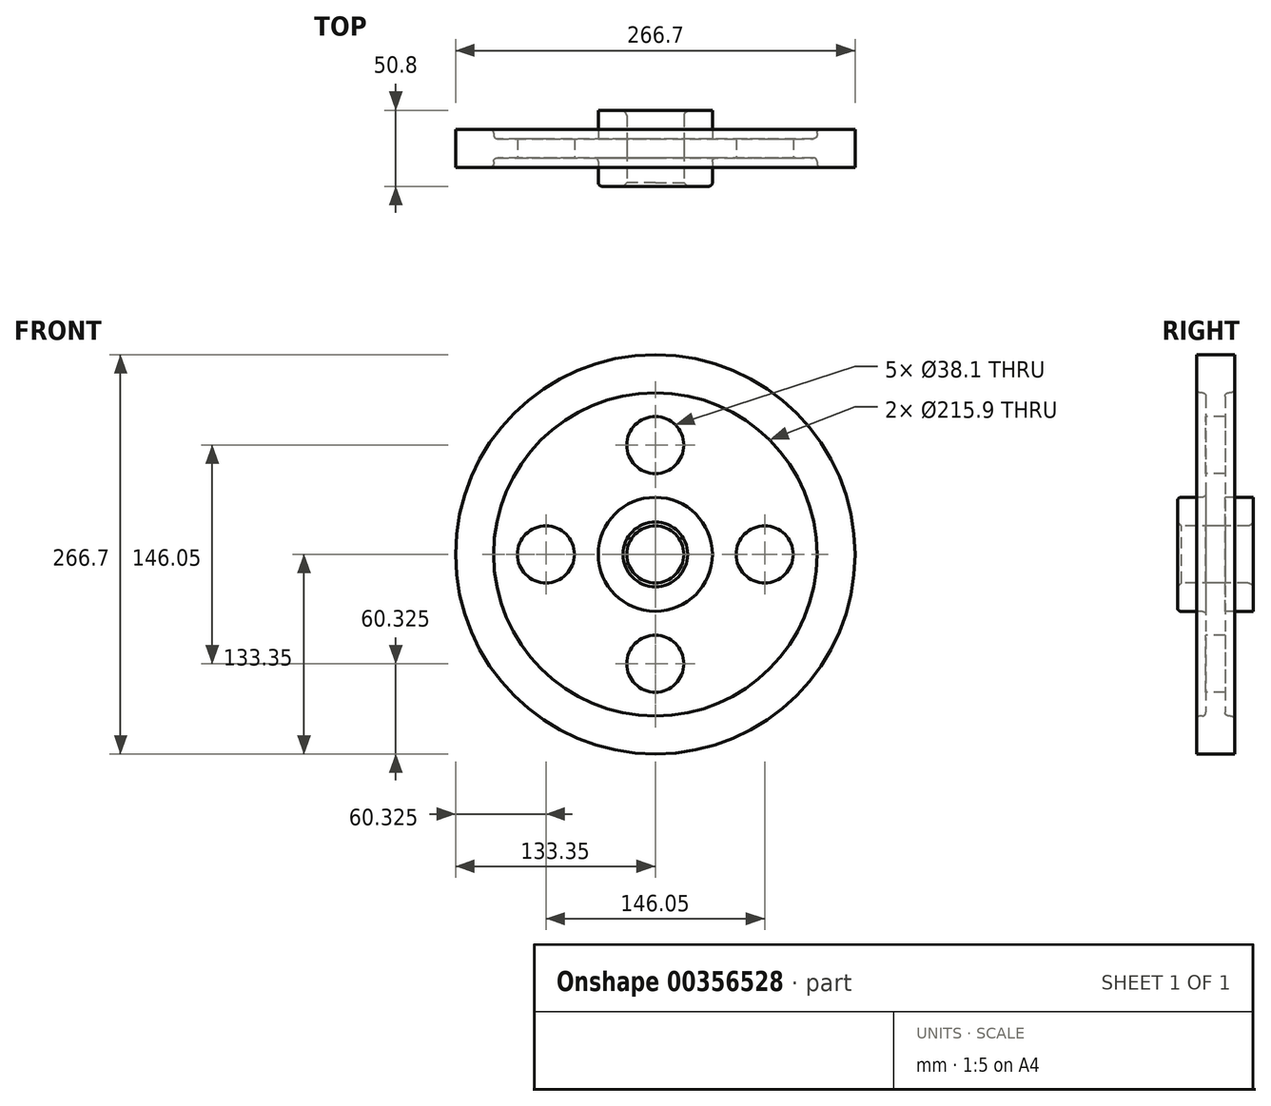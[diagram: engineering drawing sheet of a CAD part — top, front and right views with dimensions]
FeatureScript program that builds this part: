
annotation { "Feature Type Name" : "Feature", "Feature Type Description" : "" }
export const myFeature = defineFeature(function(context is Context, id is Id, definition is map)
    precondition{}
    {
        {
            var Q0;
            Q0=qCreatedBy(makeId("Right.planeOp"),FACE);
            var sketch = newSketch(context, id + "F0", { "sketchPlane" : qUnion([Q0])});
            skLineSegment(sketch, "E0", {"start": v(0, 0) * mm, "end": v(25.4, 0) * mm});
            skLineSegment(sketch, "E1.0", {"start": v(0, 19.05) * mm, "end": v(25.4, 19.05) * mm});
            skLineSegment(sketch, "E2.0", {"start": v(6.35, 38.1) * mm, "end": v(25.4, 38.1) * mm});
            skLineSegment(sketch, "E3.0", {"start": v(0, 133.35) * mm, "end": v(12.7, 133.35) * mm});
            skLineSegment(sketch, "E4.0", {"start": v(6.35, 107.95) * mm, "end": v(12.7, 107.95) * mm});
            skLineSegment(sketch, "E5", {"start": v(0, 133.35) * mm, "end": v(0, 19.05) * mm});
            skLineSegment(sketch, "E6.0", {"start": v(25.4, 38.1) * mm, "end": v(25.4, 19.05) * mm});
            skLineSegment(sketch, "E7.0", {"start": v(6.35, 107.95) * mm, "end": v(6.35, 38.1) * mm});
            skLineSegment(sketch, "E8.0", {"start": v(12.7, 133.35) * mm, "end": v(12.7, 107.95) * mm});
            skLineSegment(sketch, "E9.MirrorCS", {"start": v(-12.7, 133.35) * mm, "end": v(-12.7, 107.95) * mm});
            skLineSegment(sketch, "E10.MirrorCS", {"start": v(0, 133.35) * mm, "end": v(-12.7, 133.35) * mm});
            skLineSegment(sketch, "E11.MirrorCS", {"start": v(-6.35, 107.95) * mm, "end": v(-6.35, 38.1) * mm});
            skLineSegment(sketch, "E12.MirrorCS", {"start": v(-6.35, 107.95) * mm, "end": v(-12.7, 107.95) * mm});
            skLineSegment(sketch, "E13.MirrorCS", {"start": v(-6.35, 38.1) * mm, "end": v(-25.4, 38.1) * mm});
            skLineSegment(sketch, "E14.MirrorCS", {"start": v(-25.4, 38.1) * mm, "end": v(-25.4, 19.05) * mm});
            skLineSegment(sketch, "E15.MirrorCS", {"start": v(0, 19.05) * mm, "end": v(-25.4, 19.05) * mm});
            skSolve(sketch);
        }
        {
            var Q0;
            Q0=makeQuery(id+"F0.imprint","IMPRINT",FACE,{"disambiguationData":[TD([[makeQuery(id+"F0.imprint","IMPRINT",EDGE,{"derivedFrom":sQuery(id+"F0.wireOp",EDGE,"E1.0")}),1.0]])]});
            var Q1;
            Q1=makeQuery(id+"F0.imprint","IMPRINT",FACE,{"disambiguationData":[TD([[makeQuery(id+"F0.imprint","IMPRINT",EDGE,{"derivedFrom":sQuery(id+"F0.wireOp",EDGE,"E5")}),-1.0]])]});
            var Q2;
            Q2=sQuery(id+"F0.wireOp",EDGE,"E0");
            revolve(context, id + "F1", {"entities" : qUnion([Q0, Q1]), "axis" : qUnion([Q2]), "revolveType" : RevolveType.FULL});
        }
        {
            var Q0;
            Q0=makeQuery(id+"F1.opRevolve","SWEPT_FACE",FACE,{"disambiguationData":[OSD([sQuery(id+"F0.wireOp",EDGE,"E11.MirrorCS")])]});
            var sketch = newSketch(context, id + "F2", { "sketchPlane" : qUnion([Q0])});
            skLineSegment(sketch, "E16", {"start": v(0, 0) * mm, "end": v(0, 73.03) * mm});
            skCircle(sketch, "E17", {"center": v(0, 73.03) * mm, "radius": 19.05 * mm});
            skCircle(sketch, "E18.1.0", {"center": v(-73.03, 0) * mm, "radius": 19.05 * mm});
            skCircle(sketch, "E18.2.0", {"center": v(0, -73.03) * mm, "radius": 19.05 * mm});
            skCircle(sketch, "E18.3.0", {"center": v(73.03, 0) * mm, "radius": 19.05 * mm});
            skPoint(sketch, "E18.center", {"position": v(0, 0) * mm});
            skSolve(sketch);
        }
        {
            var Q0;
            Q0=makeQuery(id+"F2.imprint","IMPRINT",FACE,{"disambiguationData":[TD([[makeQuery(id+"F2.imprint","IMPRINT",EDGE,{"derivedFrom":sQuery(id+"F2.wireOp",EDGE,"E18.1.0")}),1.0]])]});
            var Q1;
            Q1=makeQuery(id+"F2.imprint","IMPRINT",FACE,{"disambiguationData":[TD([[makeQuery(id+"F2.imprint","IMPRINT",EDGE,{"derivedFrom":sQuery(id+"F2.wireOp",EDGE,"E18.2.0")}),1.0]])]});
            var Q2;
            Q2=makeQuery(id+"F2.imprint","IMPRINT",FACE,{"disambiguationData":[TD([[makeQuery(id+"F2.imprint","IMPRINT",EDGE,{"derivedFrom":sQuery(id+"F2.wireOp",EDGE,"E18.3.0")}),1.0]])]});
            var Q3;
            Q3=makeQuery(id+"F2.imprint","IMPRINT",FACE,{"disambiguationData":[TD([[makeQuery(id+"F2.imprint","IMPRINT",EDGE,{"derivedFrom":sQuery(id+"F2.wireOp",EDGE,"E17")}),1.0]])]});
            extrude(context, id + "F3", {"entities" : qUnion([Q0, Q1, Q2, Q3]), "operationType" : NewBodyOperationType.REMOVE, "oppositeDirection" : true, "depth" : 25.4 * mm});
        }
        {
            var Q0;
            Q0=makeQuery(id+"F1.opRevolve","SWEPT_EDGE",EDGE,{"disambiguationData":[OSD([sQuery(id+"F0.wireOp",EDGE,"E9.MirrorCS"),sQuery(id+"F0.wireOp",EDGE,"E12.MirrorCS")])]});
            var Q1;
            Q1=makeQuery(id+"F1.opRevolve","SWEPT_FACE",FACE,{"disambiguationData":[OSD([sQuery(id+"F0.wireOp",EDGE,"E13.MirrorCS")])]});
            var Q2;
            Q2=makeQuery(id+"F1.opRevolve","SWEPT_EDGE",EDGE,{"disambiguationData":[OSD([sQuery(id+"F0.wireOp",EDGE,"E13.MirrorCS"),sQuery(id+"F0.wireOp",EDGE,"E14.MirrorCS")])]});
            var Q3;
            Q3=makeQuery(id+"F1.opRevolve","SWEPT_EDGE",EDGE,{"disambiguationData":[OSD([sQuery(id+"F0.wireOp",EDGE,"E11.MirrorCS"),sQuery(id+"F0.wireOp",EDGE,"E12.MirrorCS")])]});
            fillet(context, id + "F4", {"entities" : qUnion([Q0, Q1, Q2, Q3]), "radius" : 2.54 * mm, "tangentPropagation" : true, "allowEdgeOverflow" : false});
        }
        {
            var Q0;
            Q0=makeQuery(id+"F1.opRevolve","SWEPT_EDGE",EDGE,{"disambiguationData":[OSD([sQuery(id+"F0.wireOp",EDGE,"E14.MirrorCS"),sQuery(id+"F0.wireOp",EDGE,"E15.MirrorCS")])]});
            var Q1;
            Q1=makeQuery(id+"F1.opRevolve","SWEPT_EDGE",EDGE,{"disambiguationData":[OSD([sQuery(id+"F0.wireOp",EDGE,"E1.0"),sQuery(id+"F0.wireOp",EDGE,"E6.0")])]});
            chamfer(context, id + "F5", {"entities" : qUnion([Q0, Q1]), "width" : 2.54 * mm, "tangentPropagation" : true});
        }
        {
            var Q0;
            Q0=makeQuery(id+"F1.opRevolve","SWEPT_EDGE",EDGE,{"disambiguationData":[OSD([sQuery(id+"F0.wireOp",EDGE,"E4.0"),sQuery(id+"F0.wireOp",EDGE,"E8.0")])]});
            var Q1;
            Q1=makeQuery(id+"F1.opRevolve","SWEPT_EDGE",EDGE,{"disambiguationData":[OSD([sQuery(id+"F0.wireOp",EDGE,"E4.0"),sQuery(id+"F0.wireOp",EDGE,"E7.0")])]});
            var Q2;
            {var subQ0=sQuery(id+"F0.wireOp",EDGE,"E1.0");Q2=makeQuery(id+"F5.opChamfer","BLEND_EDGE",EDGE,{"blendedFrom":[makeQuery(id+"F1.opRevolve","SWEPT_EDGE",EDGE,{"disambiguationData":[OSD([subQ0,sQuery(id+"F0.wireOp",EDGE,"E6.0")])]}),makeQuery(id+"F1.opRevolve","SWEPT_FACE",FACE,{"disambiguationData":[OSD([subQ0,sQuery(id+"F0.wireOp",EDGE,"E15.MirrorCS")])]})],"blendedInto":[makeQuery(id+"F1.opRevolve","SWEPT_FACE",FACE,{"disambiguationData":[OSD([subQ0,sQuery(id+"F0.wireOp",EDGE,"E15.MirrorCS")])]})]});}
            fillet(context, id + "F6", {"entities" : qUnion([Q0, Q1, Q2]), "radius" : 2.54 * mm, "tangentPropagation" : true, "allowEdgeOverflow" : false});
        }
    });
